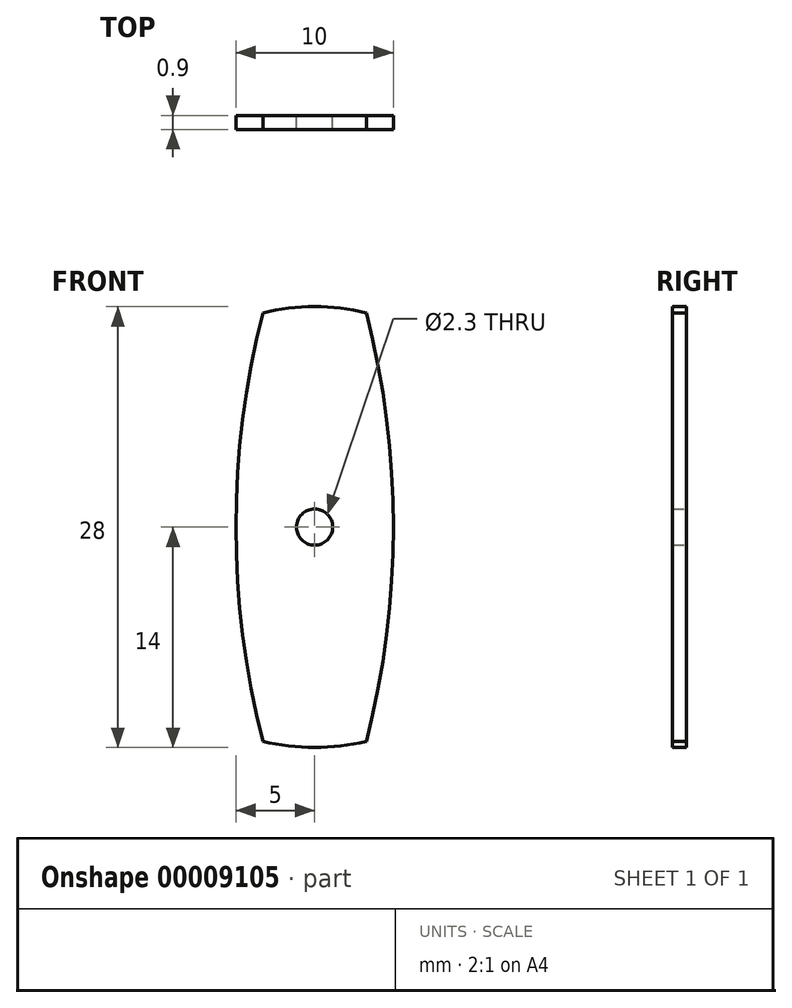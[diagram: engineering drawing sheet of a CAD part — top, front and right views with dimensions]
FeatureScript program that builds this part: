
annotation { "Feature Type Name" : "Feature", "Feature Type Description" : "" }
export const myFeature = defineFeature(function(context is Context, id is Id, definition is map)
    precondition{}
    {
        {
            var Q0;
            Q0=qCreatedBy(makeId("Front.planeOp"),FACE);
            var sketch = newSketch(context, id + "F0", { "sketchPlane" : qUnion([Q0])});
            skCircle(sketch, "E0", {"center": v(0, 0) * mm, "radius": 14 * mm});
            skCircle(sketch, "E1", {"center": v(0, 0) * mm, "radius": 1.15 * mm});
            skCircle(sketch, "E2", {"center": v(50, 0) * mm, "radius": 55 * mm});
            skCircle(sketch, "E3.MirrorC", {"center": v(-50, 0) * mm, "radius": 55 * mm});
            skSolve(sketch);
        }
        {
            var Q0;
            Q0=makeQuery(id+"F0.imprint","IMPRINT",FACE,{"disambiguationData":[TD([[makeQuery(id+"F0.imprint","IMPRINT",EDGE,{"derivedFrom":sQuery(id+"F0.wireOp",EDGE,"E1")}),-1.0]])]});
            extrude(context, id + "F1", {"entities" : qUnion([Q0]), "depth" : 0.9 * mm});
        }
    });
